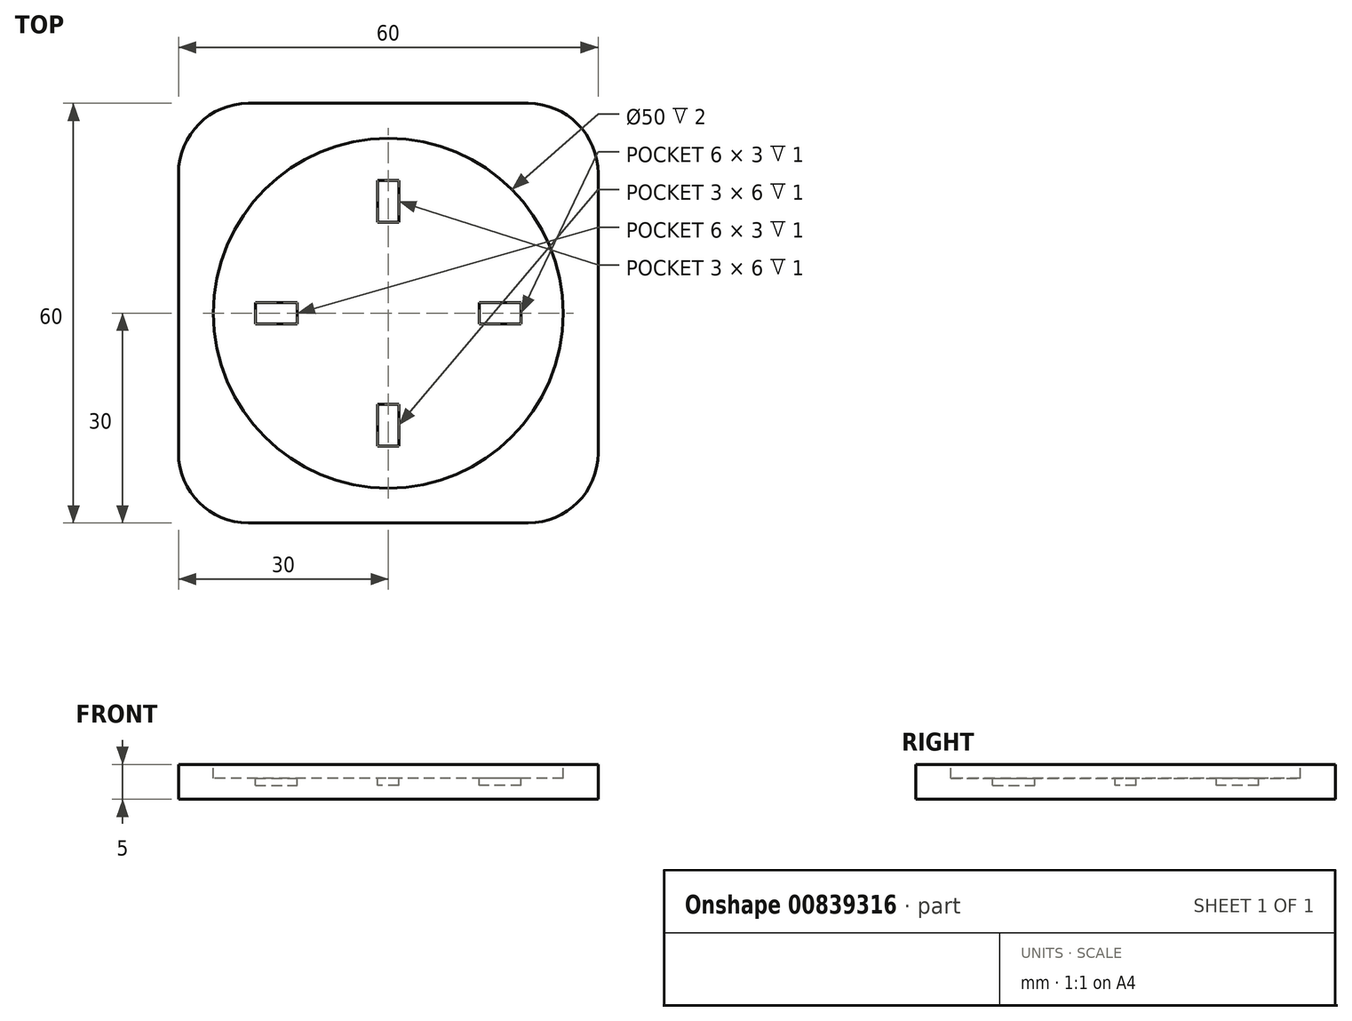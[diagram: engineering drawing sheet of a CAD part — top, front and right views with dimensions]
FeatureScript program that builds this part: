
annotation { "Feature Type Name" : "Feature", "Feature Type Description" : "" }
export const myFeature = defineFeature(function(context is Context, id is Id, definition is map)
    precondition{}
    {
        {
            var Q0;
            Q0=qCreatedBy(makeId("Top.planeOp"),FACE);
            var sketch = newSketch(context, id + "F0", { "sketchPlane" : qUnion([Q0])});
            skLineSegment(sketch, "E0.bottom", {"start": v(-30, 30) * mm, "end": v(30, 30) * mm});
            skLineSegment(sketch, "E0.top", {"start": v(-30, -30) * mm, "end": v(30, -30) * mm});
            skLineSegment(sketch, "E0.left", {"start": v(-30, 30) * mm, "end": v(-30, -30) * mm});
            skLineSegment(sketch, "E0.right", {"start": v(30, 30) * mm, "end": v(30, -30) * mm});
            skPoint(sketch, "E0.middle", {"position": v(0, 0) * mm});
            skSolve(sketch);
        }
        {
            var Q0;
            Q0 = qSketchRegion(id + "F0", true);
            extrude(context, id + "F1", {"entities" : qUnion([Q0]), "depth" : 5 * mm, "offsetDistance" : 25 * mm});
        }
        {
            var Q0;
            Q0=makeQuery(id+"F1.opExtrude","CAP_FACE",FACE,{"disambiguationData":[OSD([sQuery(id+"F0.wireOp",EDGE,"E0.bottom"),sQuery(id+"F0.wireOp",EDGE,"E0.top"),sQuery(id+"F0.wireOp",EDGE,"E0.left"),sQuery(id+"F0.wireOp",EDGE,"E0.right")])],"isStart":false});
            var sketch = newSketch(context, id + "F2", { "sketchPlane" : qUnion([Q0])});
            skCircle(sketch, "E1", {"center": v(0, 0) * mm, "radius": 25 * mm});
            skSolve(sketch);
        }
        {
            var Q0;
            Q0 = qSketchRegion(id + "F2", true);
            extrude(context, id + "F3", {"entities" : qUnion([Q0]), "operationType" : NewBodyOperationType.REMOVE, "oppositeDirection" : true, "depth" : 2 * mm, "offsetDistance" : 25 * mm});
        }
        {
            var Q0;
            Q0=makeQuery(id+"F1.opExtrude","SWEPT_EDGE",EDGE,{"disambiguationData":[OSD([sQuery(id+"F0.wireOp",EDGE,"E0.top"),sQuery(id+"F0.wireOp",EDGE,"E0.left")])]});
            var Q1;
            Q1=makeQuery(id+"F1.opExtrude","SWEPT_EDGE",EDGE,{"disambiguationData":[OSD([sQuery(id+"F0.wireOp",EDGE,"E0.top"),sQuery(id+"F0.wireOp",EDGE,"E0.right")])]});
            var Q2;
            Q2=makeQuery(id+"F1.opExtrude","SWEPT_EDGE",EDGE,{"disambiguationData":[OSD([sQuery(id+"F0.wireOp",EDGE,"E0.bottom"),sQuery(id+"F0.wireOp",EDGE,"E0.right")])]});
            var Q3;
            Q3=makeQuery(id+"F1.opExtrude","SWEPT_EDGE",EDGE,{"disambiguationData":[OSD([sQuery(id+"F0.wireOp",EDGE,"E0.bottom"),sQuery(id+"F0.wireOp",EDGE,"E0.left")])]});
            fillet(context, id + "F4", {"entities" : qUnion([Q0, Q1, Q2, Q3]), "radius" : 10 * mm, "tangentPropagation" : true, "allowEdgeOverflow" : false});
        }
        {
            var Q0;
            Q0=makeQuery(id+"F3.boolean.opBoolean","COPY",FACE,{"derivedFrom":makeQuery(id+"F3.opExtrude","CAP_FACE",FACE,{"disambiguationData":[OSD([sQuery(id+"F2.wireOp",EDGE,"E1")])],"isStart":false})});
            var sketch = newSketch(context, id + "F5", { "sketchPlane" : qUnion([Q0])});
            skLineSegment(sketch, "E2.bottom", {"start": v(-1.5, 19) * mm, "end": v(1.5, 19) * mm});
            skLineSegment(sketch, "E2.top", {"start": v(-1.5, 13) * mm, "end": v(1.5, 13) * mm});
            skLineSegment(sketch, "E2.left", {"start": v(-1.5, 19) * mm, "end": v(-1.5, 13) * mm});
            skLineSegment(sketch, "E2.right", {"start": v(1.5, 19) * mm, "end": v(1.5, 13) * mm});
            skPoint(sketch, "E2.middle", {"position": v(0, 16) * mm});
            skLineSegment(sketch, "E3.1.0", {"start": v(-19, -1.5) * mm, "end": v(-13, -1.5) * mm});
            skLineSegment(sketch, "E3.1.1", {"start": v(-19, 1.5) * mm, "end": v(-13, 1.5) * mm});
            skLineSegment(sketch, "E3.1.2", {"start": v(-19, -1.5) * mm, "end": v(-19, 1.5) * mm});
            skLineSegment(sketch, "E3.1.3", {"start": v(-13, -1.5) * mm, "end": v(-13, 1.5) * mm});
            skLineSegment(sketch, "E3.2.0", {"start": v(1.5, -19) * mm, "end": v(1.5, -13) * mm});
            skLineSegment(sketch, "E3.2.1", {"start": v(-1.5, -19) * mm, "end": v(-1.5, -13) * mm});
            skLineSegment(sketch, "E3.2.2", {"start": v(1.5, -19) * mm, "end": v(-1.5, -19) * mm});
            skLineSegment(sketch, "E3.2.3", {"start": v(1.5, -13) * mm, "end": v(-1.5, -13) * mm});
            skLineSegment(sketch, "E3.3.0", {"start": v(19, 1.5) * mm, "end": v(13, 1.5) * mm});
            skLineSegment(sketch, "E3.3.1", {"start": v(19, -1.5) * mm, "end": v(13, -1.5) * mm});
            skLineSegment(sketch, "E3.3.2", {"start": v(19, 1.5) * mm, "end": v(19, -1.5) * mm});
            skLineSegment(sketch, "E3.3.3", {"start": v(13, 1.5) * mm, "end": v(13, -1.5) * mm});
            skPoint(sketch, "E3.center", {"position": v(0, 0) * mm});
            skSolve(sketch);
        }
        {
            var Q0;
            Q0 = qSketchRegion(id + "F5", true);
            extrude(context, id + "F6", {"entities" : qUnion([Q0]), "operationType" : NewBodyOperationType.REMOVE, "oppositeDirection" : true, "depth" : 1 * mm, "offsetDistance" : 25 * mm});
        }
    });
